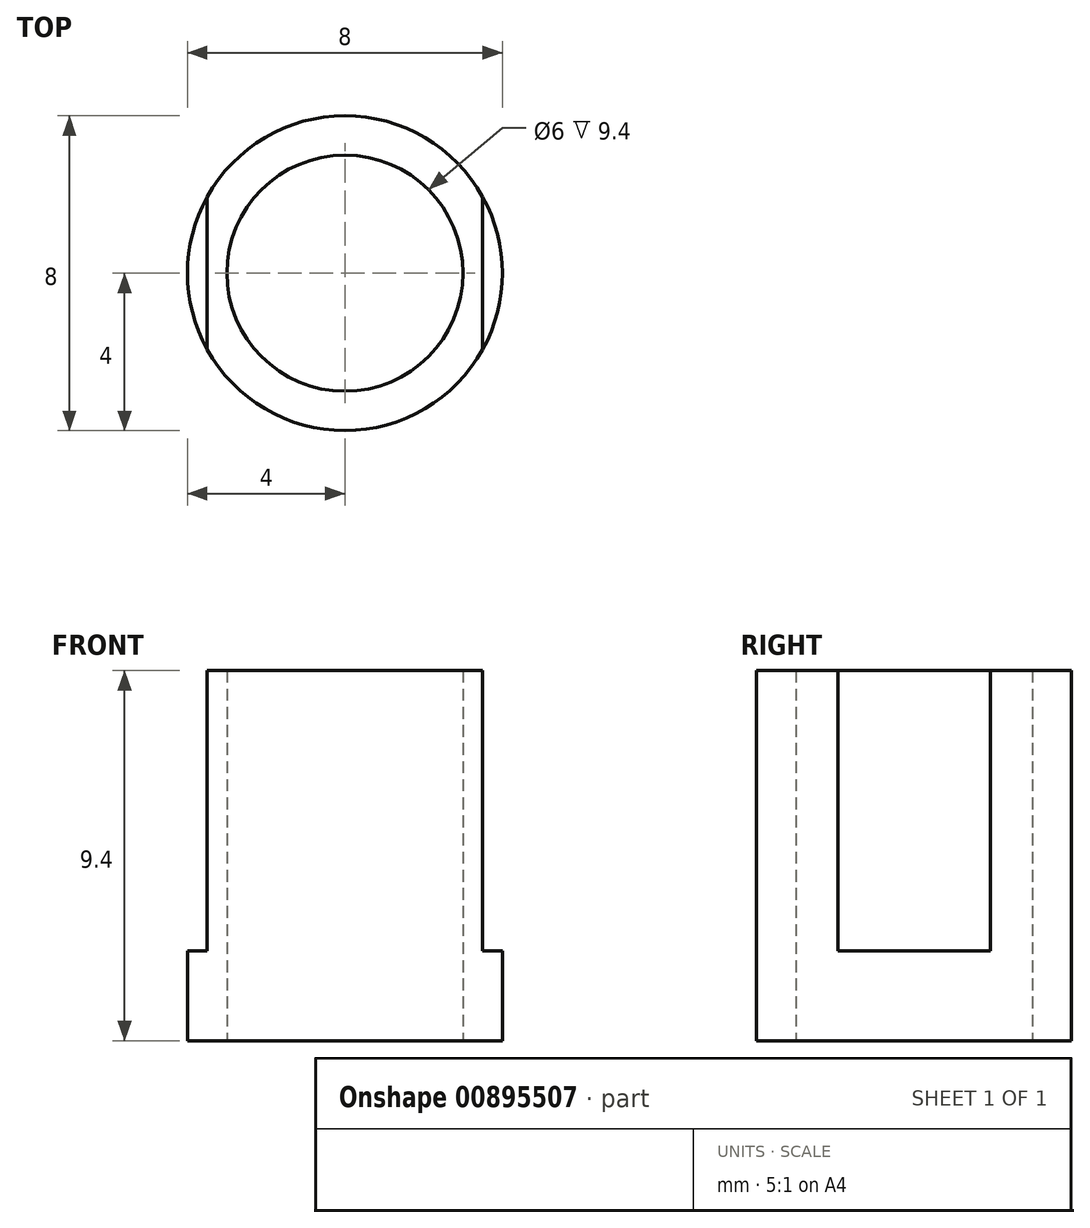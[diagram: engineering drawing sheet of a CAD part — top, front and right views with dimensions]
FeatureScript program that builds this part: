
annotation { "Feature Type Name" : "Feature", "Feature Type Description" : "" }
export const myFeature = defineFeature(function(context is Context, id is Id, definition is map)
    precondition{}
    {
        {
            var Q0;
            Q0=qCreatedBy(makeId("Top.planeOp"),FACE);
            var sketch = newSketch(context, id + "F0", { "sketchPlane" : qUnion([Q0])});
            skCircle(sketch, "E0", {"center": v(0, 0) * mm, "radius": 3 * mm});
            skCircle(sketch, "E1", {"center": v(0, 0) * mm, "radius": 4 * mm});
            skSolve(sketch);
        }
        {
            var Q0;
            Q0 = qSketchRegion(id + "F0", true);
            extrude(context, id + "F1", {"entities" : qUnion([Q0]), "depth" : 9.4 * mm, "offsetDistance" : 25 * mm});
        }
        {
            var Q0;
            Q0=makeQuery(id+"F1.opExtrude","CAP_FACE",FACE,{"disambiguationData":[OSD([sQuery(id+"F0.wireOp",EDGE,"E0"),sQuery(id+"F0.wireOp",EDGE,"E1")])],"isStart":false});
            var sketch = newSketch(context, id + "F2", { "sketchPlane" : qUnion([Q0])});
            skCircle(sketch, "E2.0", {"center": v(0, 0) * mm, "radius": 3 * mm});
            skLineSegment(sketch, "E3", {"start": v(3.5, 1.94) * mm, "end": v(3.5, -1.94) * mm});
            skLineSegment(sketch, "E4.MirrorCS", {"start": v(-3.5, 1.94) * mm, "end": v(-3.5, -1.94) * mm});
            skCircle(sketch, "E5.0", {"center": v(0, 0) * mm, "radius": 4 * mm});
            skSolve(sketch);
        }
        {
            var Q0;
            {var subQ0=sQuery(id+"F2.wireOp",EDGE,"E4.MirrorCS");Q0=makeQuery(id+"F2.imprint","IMPRINT",FACE,{"disambiguationData":[TD([[makeQuery(id+"F2.imprint","IMPRINT",EDGE,{"derivedFrom":subQ0}),-1.0]])]});}
            var Q1;
            {var subQ0=sQuery(id+"F2.wireOp",EDGE,"E3");Q1=makeQuery(id+"F2.imprint","IMPRINT",FACE,{"disambiguationData":[TD([[makeQuery(id+"F2.imprint","IMPRINT",EDGE,{"derivedFrom":subQ0}),1.0]])]});}
            extrude(context, id + "F3", {"entities" : qUnion([Q0, Q1]), "operationType" : NewBodyOperationType.REMOVE, "oppositeDirection" : true, "depth" : 7.12 * mm, "offsetDistance" : 25 * mm});
        }
    });
